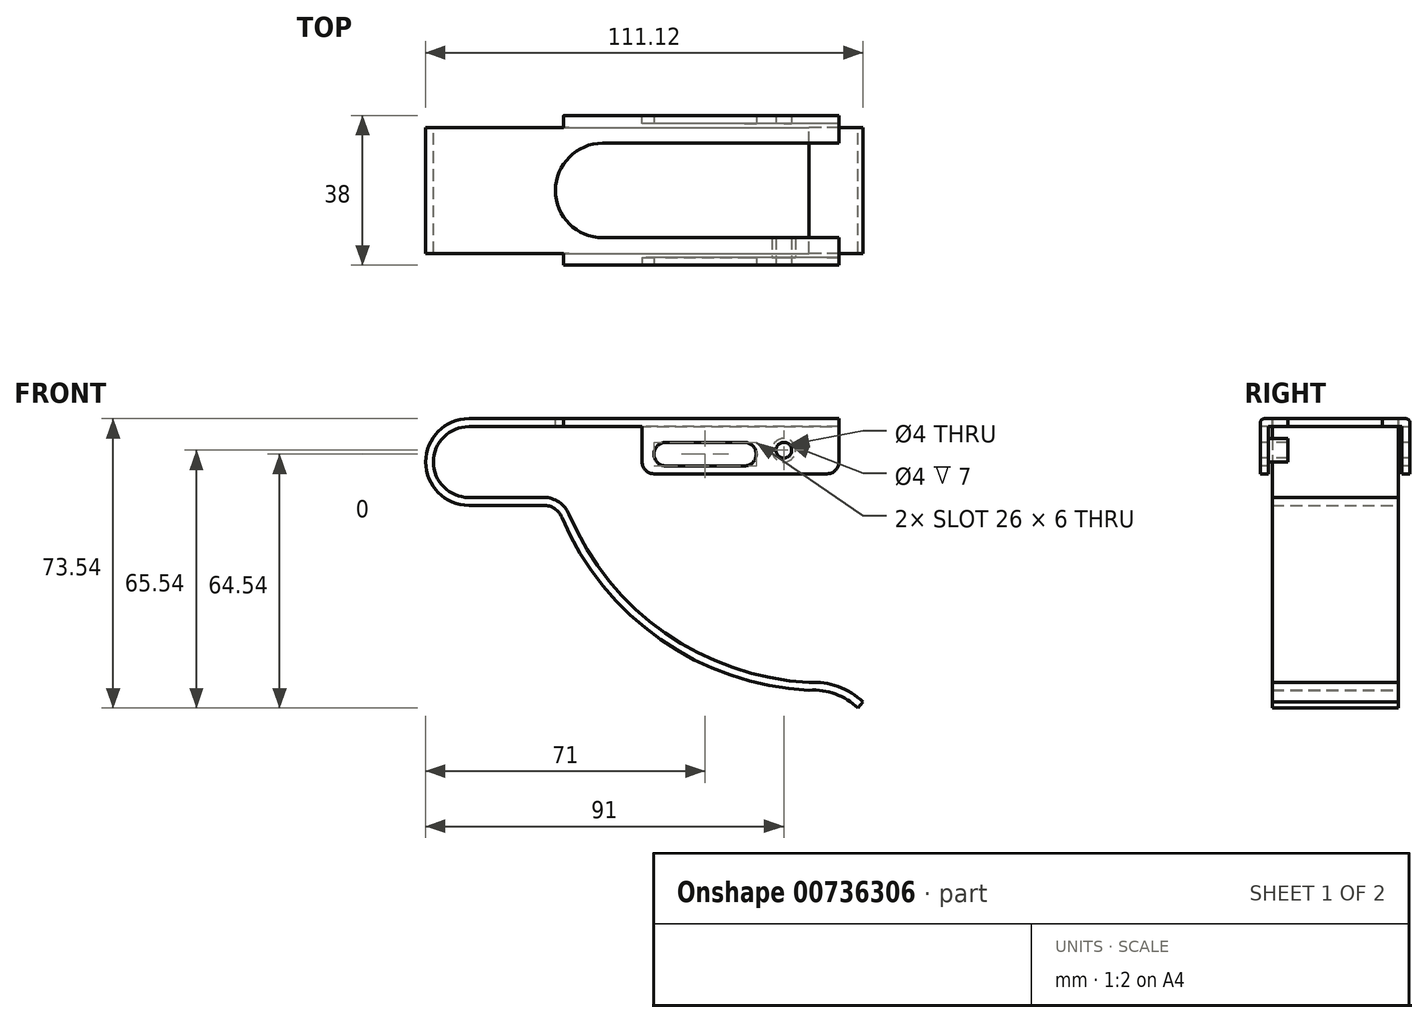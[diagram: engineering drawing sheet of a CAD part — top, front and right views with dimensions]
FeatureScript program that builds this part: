
annotation { "Feature Type Name" : "Feature", "Feature Type Description" : "" }
export const myFeature = defineFeature(function(context is Context, id is Id, definition is map)
    precondition{}
    {
        {
            var Q0;
            Q0=qCreatedBy(makeId("Front.planeOp"),FACE);
            var sketch = newSketch(context, id + "F0", { "sketchPlane" : qUnion([Q0])});
            skArc(sketch, "E0", {"start": v(0, 11) * mm, "mid": v(-11, 0) * mm, "end": v(0, -11) * mm});
            skLineSegment(sketch, "E1", {"start": v(0, 11) * mm, "end": v(94, 11) * mm});
            skLineSegment(sketch, "E2", {"start": v(0, -11) * mm, "end": v(19, -11) * mm});
            skArc(sketch, "E3", {"start": v(23.6, -14.06) * mm, "mid": v(48.7, -45.1) * mm, "end": v(86.45, -58) * mm});
            skArc(sketch, "E4", {"start": v(98.83, -62.54) * mm, "mid": v(93.13, -58.94) * mm, "end": v(86.45, -58) * mm});
            skPoint(sketch, "E5.visualSharp", {"position": v(22.4, -11) * mm});
            skArc(sketch, "E5.filletArc", {"start": v(23.6, -14.06) * mm, "mid": v(21.76, -11.83) * mm, "end": v(19, -11) * mm});
            skLineSegment(sketch, "E6.0", {"start": v(0, 9) * mm, "end": v(94, 9) * mm});
            skArc(sketch, "E6.1", {"start": v(0, 9) * mm, "mid": v(-9, 0) * mm, "end": v(0, -9) * mm});
            skArc(sketch, "E6.2", {"start": v(100.12, -61) * mm, "mid": v(93.8, -57.05) * mm, "end": v(86.43, -56) * mm});
            skArc(sketch, "E6.3", {"start": v(25.45, -13.28) * mm, "mid": v(49.79, -43.42) * mm, "end": v(86.43, -56) * mm});
            skArc(sketch, "E6.4", {"start": v(25.45, -13.28) * mm, "mid": v(22.87, -10.17) * mm, "end": v(19, -9) * mm});
            skLineSegment(sketch, "E6.5", {"start": v(0, -9) * mm, "end": v(19, -9) * mm});
            skLineSegment(sketch, "E7", {"start": v(94, 11) * mm, "end": v(94, 9) * mm});
            skLineSegment(sketch, "E8", {"start": v(100.12, -61) * mm, "end": v(98.83, -62.54) * mm});
            skLineSegment(sketch, "E9", {"start": v(100.12, -61) * mm, "end": v(153.54, -61) * mm});
            skSolve(sketch);
        }
        {
            var Q0;
            Q0 = qSketchRegion(id + "F0", true);
            extrude(context, id + "F1", {"entities" : qUnion([Q0]), "depth" : 16 * mm, "offsetDistance" : 25 * mm});
        }
        {
            var Q0;
            Q0=makeQuery(id+"F1.opExtrude","SWEPT_FACE",FACE,{"disambiguationData":[OSD([sQuery(id+"F0.wireOp",EDGE,"E1")])]});
            var sketch = newSketch(context, id + "F2", { "sketchPlane" : qUnion([Q0])});
            skLineSegment(sketch, "E10.bottom", {"start": v(94, -16) * mm, "end": v(24, -16) * mm});
            skLineSegment(sketch, "E10.top", {"start": v(94, -19) * mm, "end": v(24, -19) * mm});
            skLineSegment(sketch, "E10.left", {"start": v(94, -16) * mm, "end": v(94, -19) * mm});
            skLineSegment(sketch, "E10.right", {"start": v(24, -16) * mm, "end": v(24, -19) * mm});
            skSolve(sketch);
        }
        {
            var Q0;
            Q0=makeQuery(id+"F2.imprint","IMPRINT",FACE,{"disambiguationData":[TD([[makeQuery(id+"F2.imprint","IMPRINT",EDGE,{"derivedFrom":sQuery(id+"F2.wireOp",EDGE,"E10.bottom")}),-1.0]])]});
            extrude(context, id + "F3", {"entities" : qUnion([Q0]), "operationType" : NewBodyOperationType.ADD, "oppositeDirection" : true, "depth" : 2 * mm, "offsetDistance" : 25 * mm});
        }
        {
            var Q0;
            Q0=makeQuery(id+"F3.opExtrude","SWEPT_FACE",FACE,{"disambiguationData":[OSD([sQuery(id+"F2.wireOp",EDGE,"E10.top")])]});
            var sketch = newSketch(context, id + "F4", { "sketchPlane" : qUnion([Q0])});
            skLineSegment(sketch, "E11.bottom", {"start": v(94, 11) * mm, "end": v(44, 11) * mm});
            skLineSegment(sketch, "E11.top", {"start": v(94, -3) * mm, "end": v(44, -3) * mm});
            skLineSegment(sketch, "E11.left", {"start": v(94, 11) * mm, "end": v(94, -3) * mm});
            skLineSegment(sketch, "E11.right", {"start": v(44, 11) * mm, "end": v(44, -3) * mm});
            skSolve(sketch);
        }
        {
            var Q0;
            {var subQ0=sQuery(id+"F4.wireOp",EDGE,"E11.top");Q0=makeQuery(id+"F4.imprint","IMPRINT",FACE,{"disambiguationData":[TD([[makeQuery(id+"F4.imprint","IMPRINT",EDGE,{"derivedFrom":subQ0}),-1.0]])]});}
            extrude(context, id + "F5", {"entities" : qUnion([Q0]), "operationType" : NewBodyOperationType.ADD, "oppositeDirection" : true, "depth" : 2 * mm, "offsetDistance" : 25 * mm});
        }
        {
            var Q0;
            Q0=makeQuery(id+"F3.opExtrude","CAP_EDGE",EDGE,{"disambiguationData":[OSD([sQuery(id+"F2.wireOp",EDGE,"E10.top")])],"isStart":true});
            var Q1;
            Q1=makeQuery(id+"F5.opExtrude","CAP_EDGE",EDGE,{"disambiguationData":[OSD([sQuery(id+"F2.wireOp",EDGE,"E10.top")])],"isStart":false});
            fillet(context, id + "F6", {"entities" : qUnion([Q0, Q1]), "radius" : 1 * mm, "allowEdgeOverflow" : false});
        }
        {
            var Q0;
            Q0=makeQuery(id+"F1.opExtrude","SWEPT_BODY",BODY,{"disambiguationData":[OSD([sQuery(id+"F0.wireOp",EDGE,"E0"),sQuery(id+"F0.wireOp",EDGE,"E1"),sQuery(id+"F0.wireOp",EDGE,"E2"),sQuery(id+"F0.wireOp",EDGE,"E3"),sQuery(id+"F0.wireOp",EDGE,"E4"),sQuery(id+"F0.wireOp",EDGE,"E5.filletArc"),sQuery(id+"F0.wireOp",EDGE,"E6.0"),sQuery(id+"F0.wireOp",EDGE,"E6.1"),sQuery(id+"F0.wireOp",EDGE,"E6.2"),sQuery(id+"F0.wireOp",EDGE,"E6.3"),sQuery(id+"F0.wireOp",EDGE,"E6.4"),sQuery(id+"F0.wireOp",EDGE,"E6.5"),sQuery(id+"F0.wireOp",EDGE,"E7"),sQuery(id+"F0.wireOp",EDGE,"E8")])]});
            var Q1;
            Q1=qCreatedBy(makeId("Front.planeOp"),FACE);
            mirror(context, id + "F7", {"operationType" : NewBodyOperationType.ADD, "entities" : qUnion([Q0]), "mirrorPlane" : qUnion([Q1])});
        }
        {
            var Q0;
            {var subQ0=makeQuery(id+"F3.boolean.opBoolean","MERGE",FACE,{"derivedFrom":[makeQuery(id+"F1.opExtrude","SWEPT_FACE",FACE,{"disambiguationData":[OSD([sQuery(id+"F0.wireOp",EDGE,"E1")])]}),makeQuery(id+"F3.opExtrude","CAP_FACE",FACE,{"disambiguationData":[OSD([sQuery(id+"F2.wireOp",EDGE,"E10.bottom"),sQuery(id+"F2.wireOp",EDGE,"E10.top"),sQuery(id+"F2.wireOp",EDGE,"E10.left"),sQuery(id+"F2.wireOp",EDGE,"E10.right")])],"isStart":true})]});Q0=makeQuery(id+"F7.boolean.opBoolean","MERGE",FACE,{"derivedFrom":[subQ0,makeQuery(id+"F7.opPattern","COPY",FACE,{"derivedFrom":subQ0,"instanceName":"1"})]});}
            var sketch = newSketch(context, id + "F8", { "sketchPlane" : qUnion([Q0])});
            skLineSegment(sketch, "E12", {"start": v(34, 12) * mm, "end": v(94, 12) * mm});
            skLineSegment(sketch, "E13", {"start": v(34, -12) * mm, "end": v(94, -12) * mm});
            skLineSegment(sketch, "E14", {"start": v(94, -12) * mm, "end": v(94, 12) * mm});
            skPoint(sketch, "E15.center.orphan", {"position": v(34, 0) * mm});
            skArc(sketch, "E16", {"start": v(34, 12) * mm, "mid": v(22, 0) * mm, "end": v(34, -12) * mm});
            skSolve(sketch);
        }
        {
            var Q0;
            Q0 = qSketchRegion(id + "F8", true);
            extrude(context, id + "F9", {"entities" : qUnion([Q0]), "operationType" : NewBodyOperationType.REMOVE, "oppositeDirection" : true, "depth" : 2 * mm, "offsetDistance" : 25 * mm});
        }
        {
            var Q0;
            {var subQ0=sQuery(id+"F2.wireOp",EDGE,"E10.top");Q0=makeQuery(id+"F5.boolean.opBoolean","MERGE",FACE,{"derivedFrom":[makeQuery(id+"F3.opExtrude","SWEPT_FACE",FACE,{"disambiguationData":[OSD([subQ0])]}),makeQuery(id+"F5.opExtrude","CAP_FACE",FACE,{"disambiguationData":[OSD([subQ0,sQuery(id+"F4.wireOp",EDGE,"E11.top"),sQuery(id+"F4.wireOp",EDGE,"E11.left"),sQuery(id+"F4.wireOp",EDGE,"E11.right")])],"isStart":true})]});}
            var sketch = newSketch(context, id + "F10", { "sketchPlane" : qUnion([Q0])});
            skLineSegment(sketch, "E17", {"start": v(50, 2) * mm, "end": v(70, 2) * mm});
            skLineSegment(sketch, "E18.0", {"start": v(50, -1) * mm, "end": v(70, -1) * mm});
            skLineSegment(sketch, "E19.0", {"start": v(50, 5) * mm, "end": v(70, 5) * mm});
            skArc(sketch, "E20", {"start": v(50, 5) * mm, "mid": v(47, 2) * mm, "end": v(50, -1) * mm});
            skArc(sketch, "E21", {"start": v(70, -1) * mm, "mid": v(73, 2) * mm, "end": v(70, 5) * mm});
            skSolve(sketch);
        }
        {
            var Q0;
            Q0 = qSketchRegion(id + "F10", true);
            extrude(context, id + "F11", {"entities" : qUnion([Q0]), "operationType" : NewBodyOperationType.REMOVE, "endBound" : BoundingType.THROUGH_ALL, "oppositeDirection" : true, "depth" : 25 * mm, "offsetDistance" : 25 * mm});
        }
        {
            var Q0;
            {var subQ0=sQuery(id+"F2.wireOp",EDGE,"E10.top");Q0=makeQuery(id+"F5.boolean.opBoolean","MERGE",FACE,{"derivedFrom":[makeQuery(id+"F3.opExtrude","SWEPT_FACE",FACE,{"disambiguationData":[OSD([subQ0])]}),makeQuery(id+"F5.opExtrude","CAP_FACE",FACE,{"disambiguationData":[OSD([subQ0,sQuery(id+"F4.wireOp",EDGE,"E11.top"),sQuery(id+"F4.wireOp",EDGE,"E11.left"),sQuery(id+"F4.wireOp",EDGE,"E11.right")])],"isStart":true})]});}
            var sketch = newSketch(context, id + "F12", { "sketchPlane" : qUnion([Q0])});
            skPoint(sketch, "E22", {"position": v(80, 3) * mm});
            skSolve(sketch);
        }
        {
            var Q0;
            Q0=sQuery(id+"F12.wireOp",VERTEX,"E22");
            var Q1;
            Q1=makeQuery(id+"F1.opExtrude","SWEPT_BODY",BODY,{"disambiguationData":[OSD([sQuery(id+"F0.wireOp",EDGE,"E0"),sQuery(id+"F0.wireOp",EDGE,"E1"),sQuery(id+"F0.wireOp",EDGE,"E2"),sQuery(id+"F0.wireOp",EDGE,"E3"),sQuery(id+"F0.wireOp",EDGE,"E4"),sQuery(id+"F0.wireOp",EDGE,"E5.filletArc"),sQuery(id+"F0.wireOp",EDGE,"E6.0"),sQuery(id+"F0.wireOp",EDGE,"E6.1"),sQuery(id+"F0.wireOp",EDGE,"E6.2"),sQuery(id+"F0.wireOp",EDGE,"E6.3"),sQuery(id+"F0.wireOp",EDGE,"E6.4"),sQuery(id+"F0.wireOp",EDGE,"E6.5"),sQuery(id+"F0.wireOp",EDGE,"E7"),sQuery(id+"F0.wireOp",EDGE,"E8")])]});
            hole(context, id + "F13", {"style" : HoleStyle.SIMPLE, "endStyle" : HoleEndStyle.THROUGH, "holeDiameter" : 4 * mm, "majorDiameter" : 5 * mm, "isTappedThrough" : true, "tappedDepth" : 12 * mm, "tapClearance" : 3, "locations" : qUnion([Q0]), "scope" : qUnion([Q1])});
        }
        {
            var Q0;
            Q0=makeQuery(id+"F5.opExtrude","CAP_FACE",FACE,{"disambiguationData":[OSD([sQuery(id+"F2.wireOp",EDGE,"E10.top"),sQuery(id+"F4.wireOp",EDGE,"E11.top"),sQuery(id+"F4.wireOp",EDGE,"E11.left"),sQuery(id+"F4.wireOp",EDGE,"E11.right")])],"isStart":false});
            var sketch = newSketch(context, id + "F14", { "sketchPlane" : qUnion([Q0])});
            skCircle(sketch, "E23.0", {"center": v(-80, 3) * mm, "radius": 2 * mm});
            skCircle(sketch, "E24.0", {"center": v(-80, 3) * mm, "radius": 3 * mm});
            skSolve(sketch);
        }
        {
            var Q0;
            Q0 = qSketchRegion(id + "F14", true);
            extrude(context, id + "F15", {"entities" : qUnion([Q0]), "operationType" : NewBodyOperationType.ADD, "depth" : 5 * mm, "offsetDistance" : 25 * mm});
        }
        {
            var Q0;
            Q0=makeQuery(id+"F7.opPattern","COPY",EDGE,{"derivedFrom":makeQuery(id+"F5.opExtrude","SWEPT_EDGE",EDGE,{"disambiguationData":[OSD([sQuery(id+"F4.wireOp",EDGE,"E11.top"),sQuery(id+"F4.wireOp",EDGE,"E11.left")])]}),"instanceName":"1"});
            var Q1;
            Q1=makeQuery(id+"F7.opPattern","COPY",EDGE,{"derivedFrom":makeQuery(id+"F5.opExtrude","SWEPT_EDGE",EDGE,{"disambiguationData":[OSD([sQuery(id+"F4.wireOp",EDGE,"E11.top"),sQuery(id+"F4.wireOp",EDGE,"E11.right")])]}),"instanceName":"1"});
            var Q2;
            Q2=makeQuery(id+"F5.opExtrude","SWEPT_EDGE",EDGE,{"disambiguationData":[OSD([sQuery(id+"F4.wireOp",EDGE,"E11.top"),sQuery(id+"F4.wireOp",EDGE,"E11.right")])]});
            var Q3;
            Q3=makeQuery(id+"F5.opExtrude","SWEPT_EDGE",EDGE,{"disambiguationData":[OSD([sQuery(id+"F4.wireOp",EDGE,"E11.top"),sQuery(id+"F4.wireOp",EDGE,"E11.left")])]});
            fillet(context, id + "F16", {"entities" : qUnion([Q0, Q1, Q2, Q3]), "radius" : 3 * mm, "tangentPropagation" : true, "allowEdgeOverflow" : false});
        }
    });
